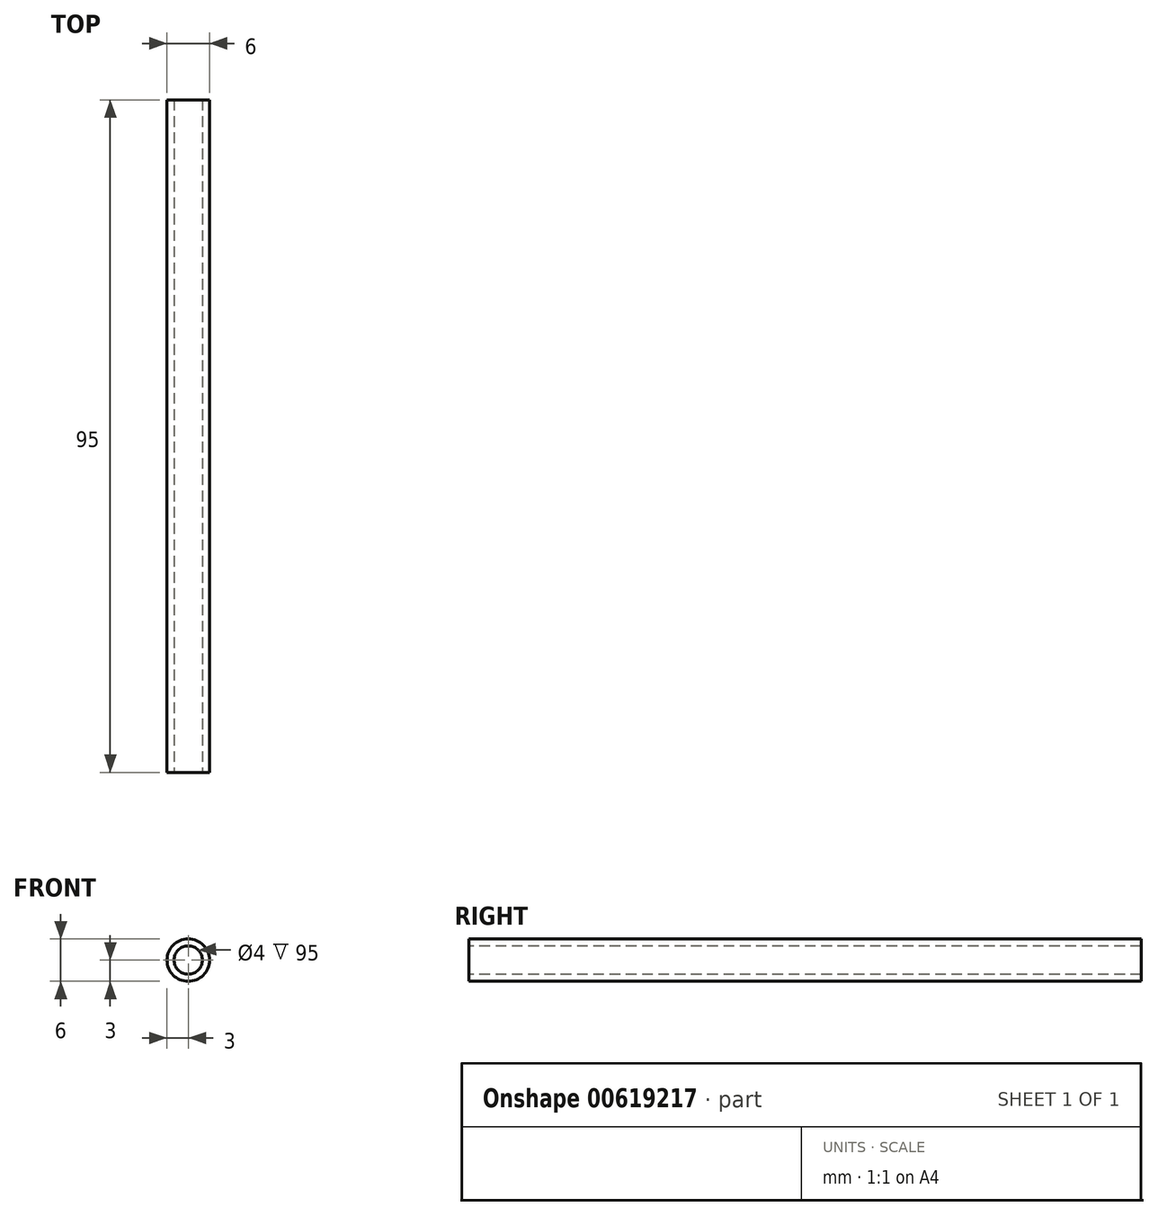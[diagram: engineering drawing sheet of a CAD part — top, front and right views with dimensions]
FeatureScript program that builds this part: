
annotation { "Feature Type Name" : "Feature", "Feature Type Description" : "" }
export const myFeature = defineFeature(function(context is Context, id is Id, definition is map)
    precondition{}
    {
        {
            var Q0;
            Q0=qCreatedBy(makeId("Front.planeOp"),FACE);
            var sketch = newSketch(context, id + "F0", { "sketchPlane" : qUnion([Q0])});
            skCircle(sketch, "E0", {"center": v(0, 0) * mm, "radius": 3 * mm});
            skSolve(sketch);
        }
        {
            var Q0;
            Q0=qSketchRegion(id+"F0",true);
            extrude(context, id + "F1", {"entities" : qUnion([Q0]), "depth" : 95 * mm, "offsetDistance" : 25.4 * mm});
        }
        {
            var Q0;
            Q0=makeQuery(id+"F1.opExtrude","CAP_FACE",FACE,{"disambiguationData":[OSD([sQuery(id+"F0.wireOp",EDGE,"E0")])],"isStart":false});
            var sketch = newSketch(context, id + "F2", { "sketchPlane" : qUnion([Q0])});
            skCircle(sketch, "E1", {"center": v(0, 0) * mm, "radius": 2 * mm, "construction": true});
            skSolve(sketch);
        }
        {
            var Q0;
            Q0=sQuery(id+"F2.wireOp",VERTEX,"E1.center");
            var Q1;
            Q1=makeQuery(id+"F1.opExtrude","SWEPT_BODY",BODY,{"disambiguationData":[OSD([sQuery(id+"F0.wireOp",EDGE,"E0")])]});
            hole(context, id + "F3", {"style" : HoleStyle.SIMPLE, "endStyle" : HoleEndStyle.THROUGH, "holeDiameter" : 4 * mm, "majorDiameter" : 6.35 * mm, "isTappedThrough" : true, "tappedDepth" : 12.7 * mm, "tapClearance" : 3, "locations" : qUnion([Q0]), "scope" : qUnion([Q1])});
        }
    });
